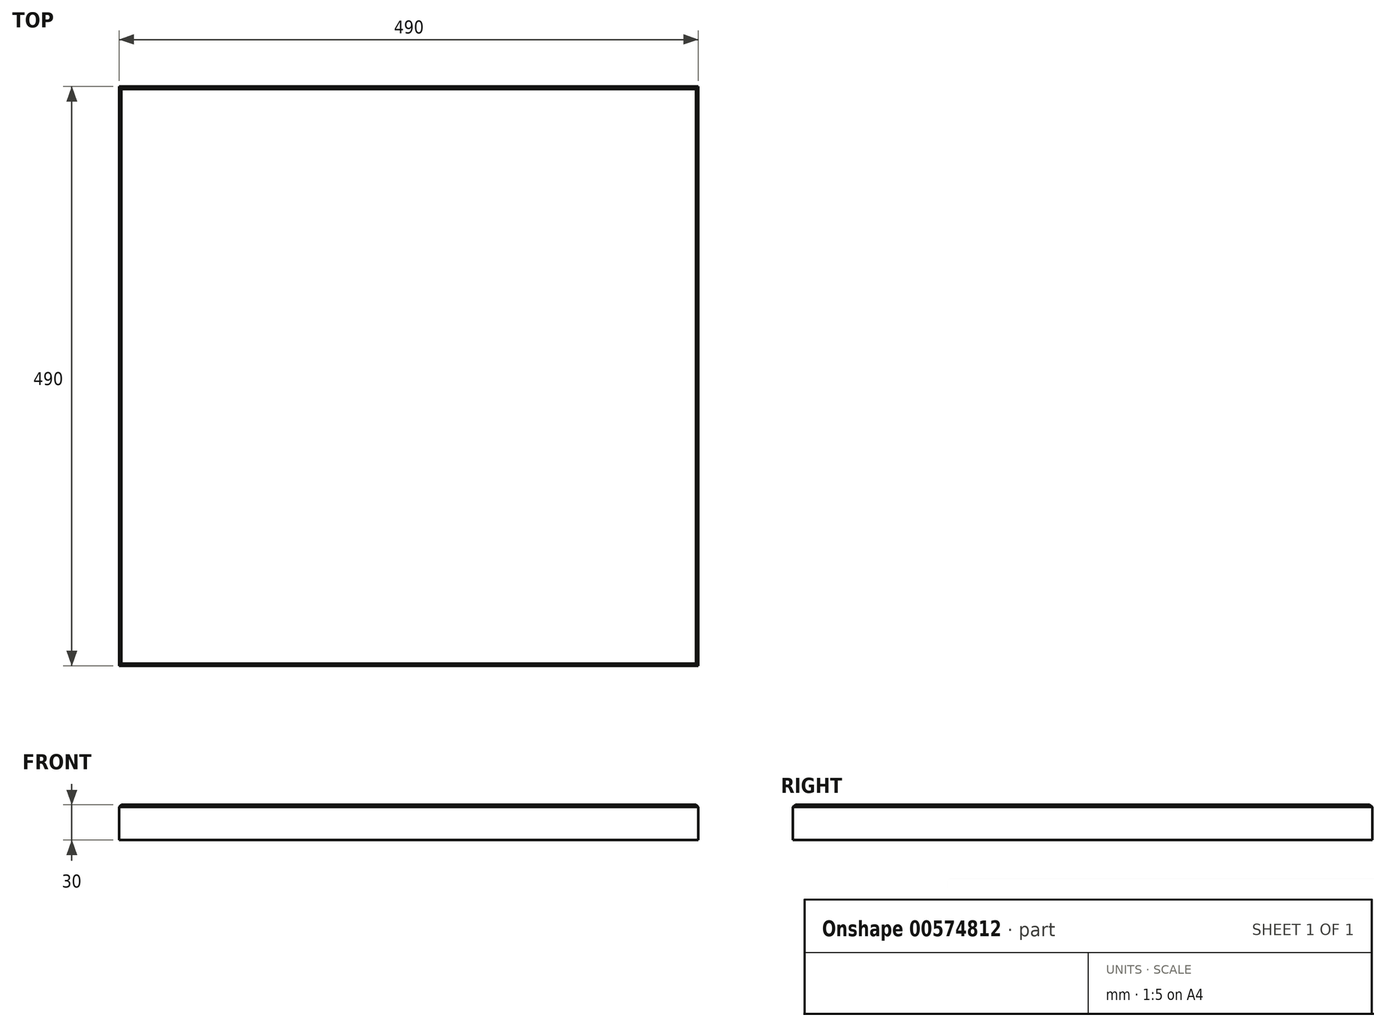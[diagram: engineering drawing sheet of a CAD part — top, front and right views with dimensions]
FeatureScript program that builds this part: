
annotation { "Feature Type Name" : "Feature", "Feature Type Description" : "" }
export const myFeature = defineFeature(function(context is Context, id is Id, definition is map)
    precondition{}
    {
        {
            var Q0;
            Q0=qCreatedBy(makeId("Top.planeOp"),FACE);
            var sketch = newSketch(context, id + "F0", { "sketchPlane" : qUnion([Q0])});
            skLineSegment(sketch, "E0.bottom", {"start": v(-245, 245) * mm, "end": v(245, 245) * mm});
            skLineSegment(sketch, "E0.top", {"start": v(-245, -245) * mm, "end": v(245, -245) * mm});
            skLineSegment(sketch, "E0.left", {"start": v(-245, 245) * mm, "end": v(-245, -245) * mm});
            skLineSegment(sketch, "E0.right", {"start": v(245, 245) * mm, "end": v(245, -245) * mm});
            skSolve(sketch);
        }
        {
            var Q0;
            Q0=makeQuery(id+"F0.imprint","IMPRINT",FACE,{"disambiguationData":[TD([[makeQuery(id+"F0.imprint","IMPRINT",EDGE,{"derivedFrom":sQuery(id+"F0.wireOp",EDGE,"E0.bottom")}),-1.0]])]});
            extrude(context, id + "F1", {"entities" : qUnion([Q0]), "depth" : 30 * mm, "offsetDistance" : 25 * mm});
        }
        {
            var Q0;
            Q0=makeQuery(id+"F1.opExtrude","CAP_EDGE",EDGE,{"disambiguationData":[OSD([sQuery(id+"F0.wireOp",EDGE,"E0.left")])],"isStart":false});
            var Q1;
            Q1=makeQuery(id+"F1.opExtrude","CAP_EDGE",EDGE,{"disambiguationData":[OSD([sQuery(id+"F0.wireOp",EDGE,"E0.top")])],"isStart":false});
            var Q2;
            Q2=makeQuery(id+"F1.opExtrude","CAP_EDGE",EDGE,{"disambiguationData":[OSD([sQuery(id+"F0.wireOp",EDGE,"E0.right")])],"isStart":false});
            var Q3;
            Q3=makeQuery(id+"F1.opExtrude","CAP_EDGE",EDGE,{"disambiguationData":[OSD([sQuery(id+"F0.wireOp",EDGE,"E0.bottom")])],"isStart":false});
            chamfer(context, id + "F2", {"entities" : qUnion([Q0, Q1, Q2, Q3]), "width" : 2 * mm, "tangentPropagation" : true});
        }
    });
